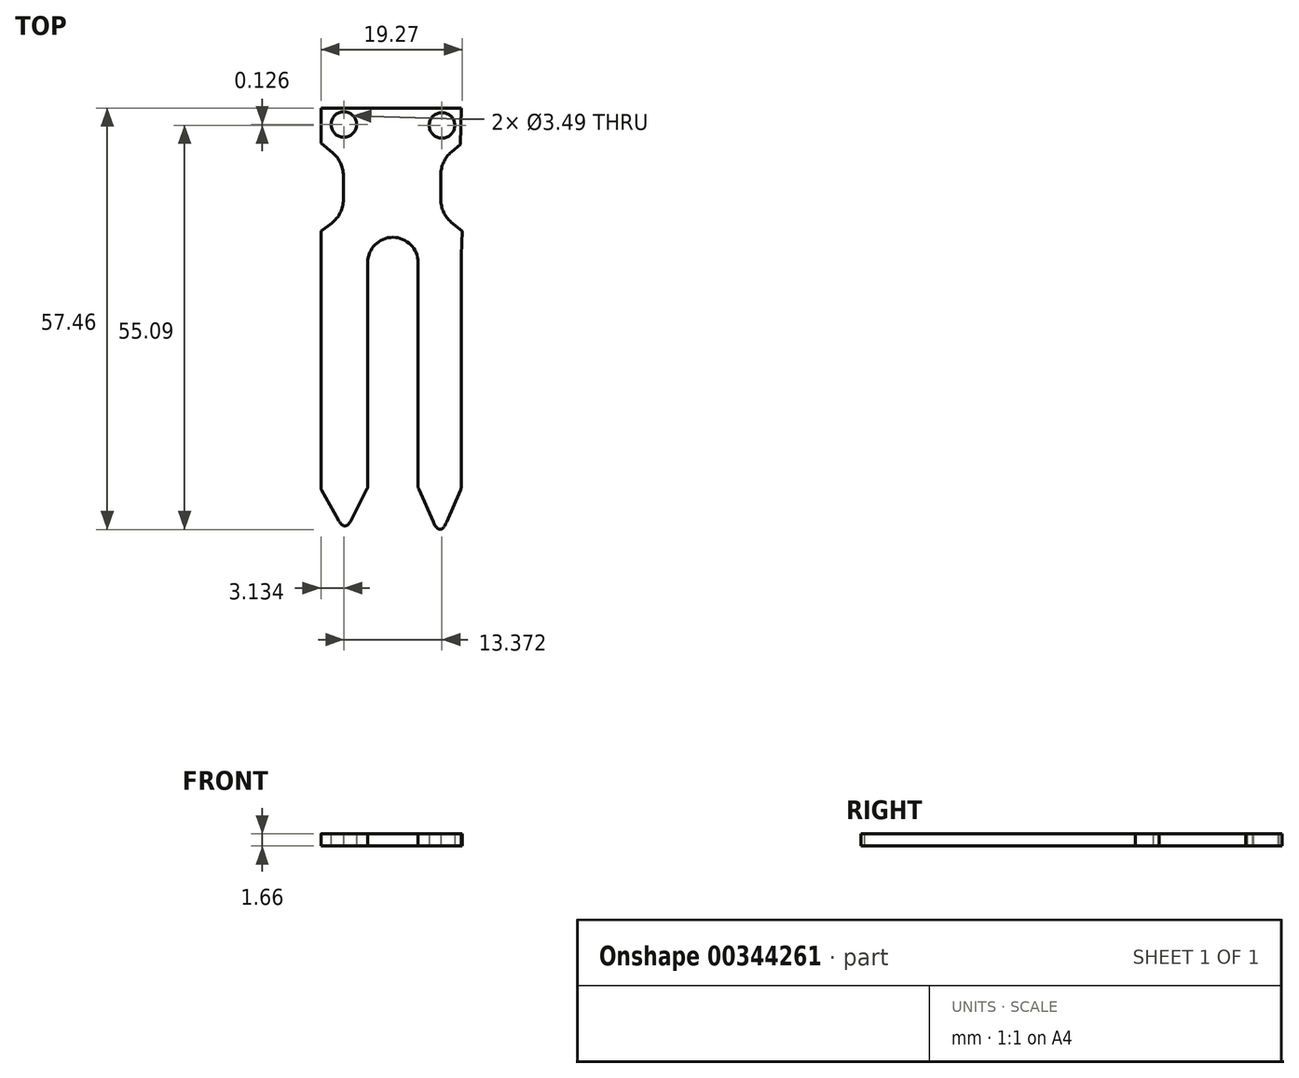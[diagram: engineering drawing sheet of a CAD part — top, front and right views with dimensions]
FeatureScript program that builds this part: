
annotation { "Feature Type Name" : "Feature", "Feature Type Description" : "" }
export const myFeature = defineFeature(function(context is Context, id is Id, definition is map)
    precondition{}
    {
        {
            var Q0;
            Q0=qCreatedBy(makeId("Top.planeOp"),FACE);
            var sketch = newSketch(context, id + "F0", { "sketchPlane" : qUnion([Q0])});
            skLineSegment(sketch, "E0.left", {"start": v(-9.82, 21.07) * mm, "end": v(-9.82, 16.27) * mm});
            skLineSegment(sketch, "E1", {"start": v(-9.82, -30.82) * mm, "end": v(-6.52, -36.75) * mm});
            skLineSegment(sketch, "E2", {"start": v(-6.52, -36.75) * mm, "end": v(-3.43, -30.7) * mm});
            skLineSegment(sketch, "E3", {"start": v(-9.82, -30.82) * mm, "end": v(-9.82, 0.88) * mm});
            skLineSegment(sketch, "E4", {"start": v(-3.43, -30.7) * mm, "end": v(-3.43, 0) * mm});
            skLineSegment(sketch, "E5.MirrorCS", {"start": v(3.43, -30.82) * mm, "end": v(3.43, 0) * mm});
            skLineSegment(sketch, "E6.MirrorCS", {"start": v(9.3, 1) * mm, "end": v(9.3, 1) * mm});
            skLineSegment(sketch, "E7", {"start": v(-9.82, 0.88) * mm, "end": v(-9.82, 4.26) * mm});
            skArc(sketch, "E8", {"start": v(-3.43, 0) * mm, "mid": v(0, 3.43) * mm, "end": v(3.43, 0) * mm});
            skLineSegment(sketch, "E9", {"start": v(-6.76, 6.6) * mm, "end": v(-6.76, 13.74) * mm});
            skLineSegment(sketch, "E10", {"start": v(-9.82, 4.26) * mm, "end": v(-6.76, 6.6) * mm});
            skLineSegment(sketch, "E11", {"start": v(-6.76, 13.74) * mm, "end": v(-9.82, 16.27) * mm});
            skLineSegment(sketch, "E12.MirrorCS", {"start": v(6.54, 13.87) * mm, "end": v(9.22, 16.09) * mm});
            skLineSegment(sketch, "E13.MirrorCS", {"start": v(6.54, 6.72) * mm, "end": v(6.54, 13.87) * mm});
            skLineSegment(sketch, "E14.MirrorCS", {"start": v(9.45, 4.26) * mm, "end": v(6.54, 6.72) * mm});
            skLineSegment(sketch, "E15", {"start": v(9.22, 16.09) * mm, "end": v(9.3, 21.07) * mm});
            skLineSegment(sketch, "E16", {"start": v(-9.82, 21.07) * mm, "end": v(9.3, 21.07) * mm});
            skCircle(sketch, "E17", {"center": v(6.69, 18.7) * mm, "radius": 1.75 * mm});
            skPoint(sketch, "E18.startSnap0", {"position": v(-0.26, 21.07) * mm});
            skPoint(sketch, "E19.orphan", {"position": v(-9.82, 32.58) * mm});
            skPoint(sketch, "E20.orphan", {"position": v(0, 21.07) * mm});
            skLineSegment(sketch, "E21.trimOffspring", {"start": v(-9.82, -30.82) * mm, "end": v(-9.82, -30.82) * mm});
            skLineSegment(sketch, "E22.trimOffspring", {"start": v(-9.82, 4.26) * mm, "end": v(-9.82, -30.82) * mm});
            skLineSegment(sketch, "E23.MirrorCS", {"start": v(9.3, -30.88) * mm, "end": v(6.42, -37.42) * mm});
            skLineSegment(sketch, "E24.MirrorCS", {"start": v(6.42, -37.42) * mm, "end": v(3.43, -30.7) * mm});
            skCircle(sketch, "E25.MirrorC", {"center": v(-6.69, 18.83) * mm, "radius": 1.75 * mm});
            skLineSegment(sketch, "E26", {"start": v(9.45, 4.26) * mm, "end": v(9.3, 1) * mm});
            skLineSegment(sketch, "E27", {"start": v(9.3, -30.88) * mm, "end": v(9.3, 1) * mm});
            skSolve(sketch);
        }
        {
            var Q0;
            Q0 = qSketchRegion(id + "F0", true);
            extrude(context, id + "F1", {"entities" : qUnion([Q0]), "depth" : 1.66 * mm});
        }
        {
            var Q0;
            Q0=makeQuery(id+"F1.opExtrude","SWEPT_EDGE",EDGE,{"disambiguationData":[OSD([sQuery(id+"F0.wireOp",EDGE,"E9"),sQuery(id+"F0.wireOp",EDGE,"E10")])]});
            var Q1;
            Q1=makeQuery(id+"F1.opExtrude","SWEPT_EDGE",EDGE,{"disambiguationData":[OSD([sQuery(id+"F0.wireOp",EDGE,"E9"),sQuery(id+"F0.wireOp",EDGE,"E11")])]});
            var Q2;
            Q2=makeQuery(id+"F1.opExtrude","SWEPT_EDGE",EDGE,{"disambiguationData":[OSD([sQuery(id+"F0.wireOp",EDGE,"E13.MirrorCS"),sQuery(id+"F0.wireOp",EDGE,"E14.MirrorCS")])]});
            var Q3;
            Q3=makeQuery(id+"F1.opExtrude","SWEPT_EDGE",EDGE,{"disambiguationData":[OSD([sQuery(id+"F0.wireOp",EDGE,"E12.MirrorCS"),sQuery(id+"F0.wireOp",EDGE,"E13.MirrorCS")])]});
            fillet(context, id + "F2", {"entities" : qUnion([Q0, Q1, Q2, Q3]), "radius" : 4 * mm, "tangentPropagation" : true, "allowEdgeOverflow" : false});
        }
        {
            var Q0;
            Q0=makeQuery(id+"F1.opExtrude","SWEPT_EDGE",EDGE,{"disambiguationData":[OSD([sQuery(id+"F0.wireOp",EDGE,"E1"),sQuery(id+"F0.wireOp",EDGE,"E2")])]});
            var Q1;
            Q1=makeQuery(id+"F1.opExtrude","SWEPT_EDGE",EDGE,{"disambiguationData":[OSD([sQuery(id+"F0.wireOp",EDGE,"E1"),sQuery(id+"F0.wireOp",EDGE,"E22.trimOffspring")])]});
            var Q2;
            Q2=makeQuery(id+"F1.opExtrude","SWEPT_EDGE",EDGE,{"disambiguationData":[OSD([sQuery(id+"F0.wireOp",EDGE,"E5.MirrorCS"),sQuery(id+"F0.wireOp",EDGE,"E24.MirrorCS")])]});
            var Q3;
            Q3=makeQuery(id+"F1.opExtrude","SWEPT_EDGE",EDGE,{"disambiguationData":[OSD([sQuery(id+"F0.wireOp",EDGE,"E23.MirrorCS"),sQuery(id+"F0.wireOp",EDGE,"E24.MirrorCS")])]});
            var Q4;
            Q4=makeQuery(id+"F1.opExtrude","SWEPT_EDGE",EDGE,{"disambiguationData":[OSD([sQuery(id+"F0.wireOp",EDGE,"E2"),sQuery(id+"F0.wireOp",EDGE,"E4")])]});
            var Q5;
            Q5=makeQuery(id+"F1.opExtrude","SWEPT_EDGE",EDGE,{"disambiguationData":[OSD([sQuery(id+"F0.wireOp",EDGE,"E0.right"),sQuery(id+"F0.wireOp",EDGE,"E23.MirrorCS")])]});
            fillet(context, id + "F3", {"entities" : qUnion([Q0, Q1, Q2, Q3, Q4, Q5]), "radius" : 1 * mm, "tangentPropagation" : true, "rho" : 0.5, "crossSection" : FilletCrossSection.CONIC, "allowEdgeOverflow" : false});
        }
    });
